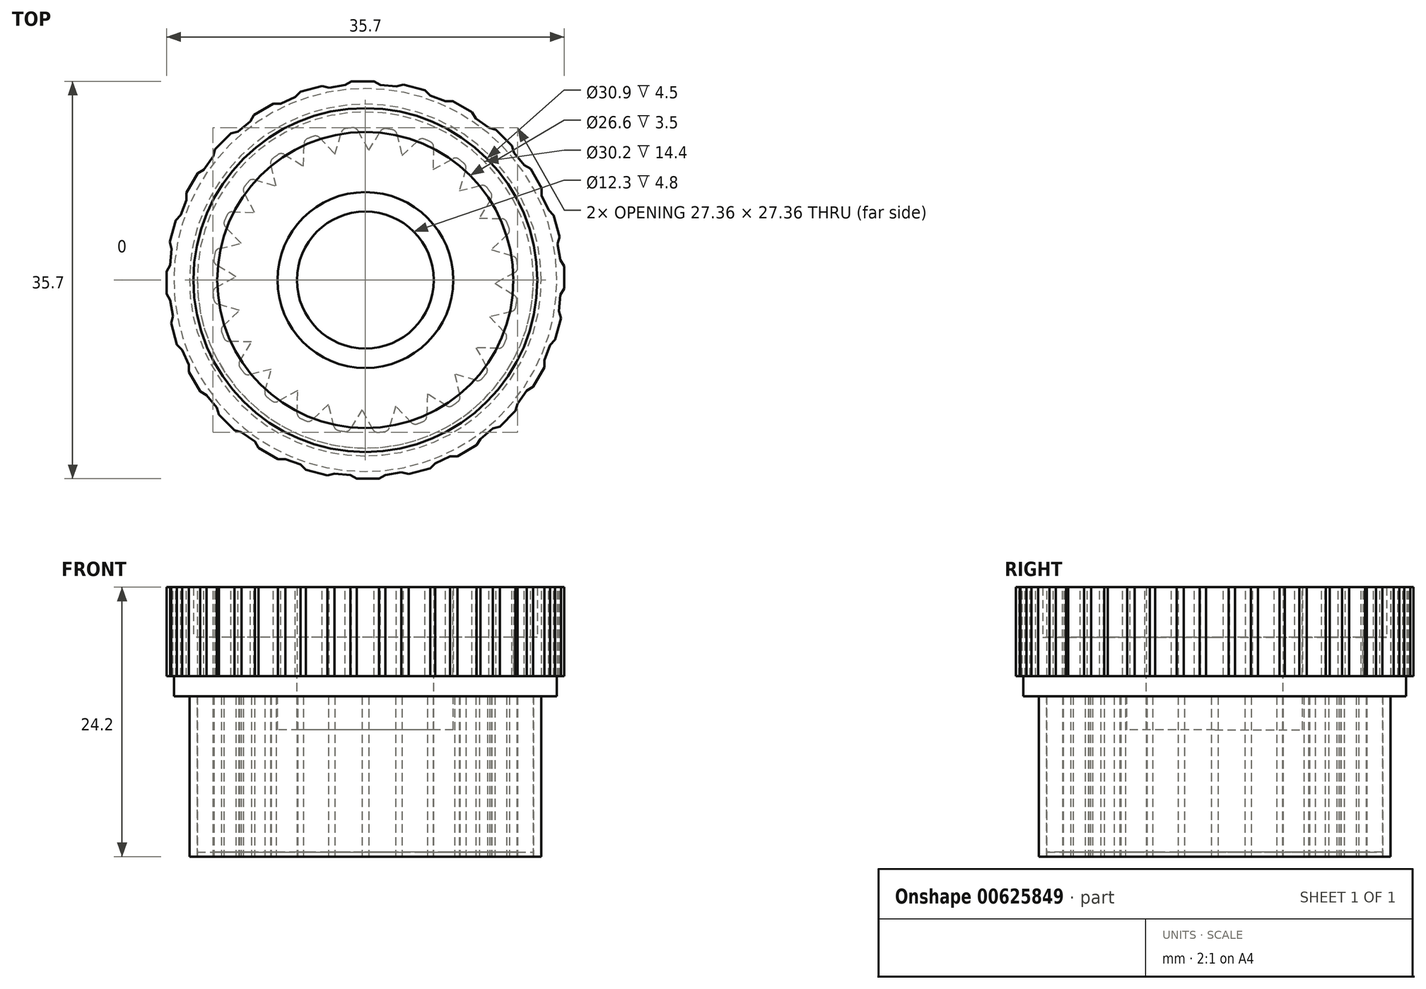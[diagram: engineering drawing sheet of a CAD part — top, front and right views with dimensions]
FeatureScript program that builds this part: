
annotation { "Feature Type Name" : "Feature", "Feature Type Description" : "" }
export const myFeature = defineFeature(function(context is Context, id is Id, definition is map)
    precondition{}
    {
        {
            var Q0;
            Q0=qCreatedBy(makeId("Top.planeOp"),FACE);
            var sketch = newSketch(context, id + "F0", { "sketchPlane" : qUnion([Q0])});
            skCircle(sketch, "E0", {"center": v(0, 0) * mm, "radius": 17.2 * mm});
            skCircle(sketch, "E1", {"center": v(0, 0) * mm, "radius": 15.45 * mm});
            skCircle(sketch, "E2", {"center": v(0, 0) * mm, "radius": 13.3 * mm});
            skCircle(sketch, "E3", {"center": v(0, 0) * mm, "radius": 6.15 * mm});
            skCircle(sketch, "E4", {"center": v(0, 0) * mm, "radius": 7.9 * mm});
            skSolve(sketch);
        }
        {
            var Q0;
            Q0=qSketchRegion(id+"F0",true);
            extrude(context, id + "F1", {"entities" : qUnion([Q0]), "depth" : 8 * mm, "offsetDistance" : 25 * mm});
        }
        {
            var Q0;
            Q0=makeQuery(id+"F0.imprint","IMPRINT",FACE,{"disambiguationData":[TD([[makeQuery(id+"F0.imprint","IMPRINT",EDGE,{"derivedFrom":sQuery(id+"F0.wireOp",EDGE,"E1")}),1.0]])]});
            extrude(context, id + "F2", {"entities" : qUnion([Q0]), "operationType" : NewBodyOperationType.ADD, "depth" : 3.5 * mm, "offsetDistance" : 25 * mm});
        }
        {
            var Q0;
            Q0=makeQuery(id+"F0.imprint","IMPRINT",FACE,{"disambiguationData":[TD([[makeQuery(id+"F0.imprint","IMPRINT",EDGE,{"derivedFrom":sQuery(id+"F0.wireOp",EDGE,"E3")}),-1.0]])]});
            extrude(context, id + "F3", {"entities" : qUnion([Q0]), "depth" : 8 * mm, "offsetDistance" : 25 * mm});
        }
        {
            var Q0;
            Q0=makeQuery(id+"F0.imprint","IMPRINT",FACE,{"disambiguationData":[TD([[makeQuery(id+"F0.imprint","IMPRINT",EDGE,{"derivedFrom":sQuery(id+"F0.wireOp",EDGE,"E0")}),1.0]])]});
            var Q1;
            Q1=makeQuery(id+"F0.imprint","IMPRINT",FACE,{"disambiguationData":[TD([[makeQuery(id+"F0.imprint","IMPRINT",EDGE,{"derivedFrom":sQuery(id+"F0.wireOp",EDGE,"E1")}),1.0]])]});
            var Q2;
            Q2=makeQuery(id+"F0.imprint","IMPRINT",FACE,{"disambiguationData":[TD([[makeQuery(id+"F0.imprint","IMPRINT",EDGE,{"derivedFrom":sQuery(id+"F0.wireOp",EDGE,"E2")}),1.0]])]});
            var Q3;
            Q3=makeQuery(id+"F0.imprint","IMPRINT",FACE,{"disambiguationData":[TD([[makeQuery(id+"F0.imprint","IMPRINT",EDGE,{"derivedFrom":sQuery(id+"F0.wireOp",EDGE,"E3")}),-1.0]])]});
            var Q4;
            Q4=makeQuery(id+"F0.imprint","IMPRINT",FACE,{"disambiguationData":[TD([[makeQuery(id+"F0.imprint","IMPRINT",EDGE,{"derivedFrom":sQuery(id+"F0.wireOp",EDGE,"E3")}),1.0]])]});
            extrude(context, id + "F4", {"entities" : qUnion([Q0, Q1, Q2, Q3, Q4]), "oppositeDirection" : true, "depth" : 1.8 * mm, "offsetDistance" : 25 * mm});
        }
        {
            var Q0;
            Q0=makeQuery(id+"F4.opExtrude","CAP_FACE",FACE,{"disambiguationData":[OSD([sQuery(id+"F0.wireOp",EDGE,"E0")])],"isStart":false});
            var sketch = newSketch(context, id + "F5", { "sketchPlane" : qUnion([Q0])});
            skCircle(sketch, "E5", {"center": v(0, 0) * mm, "radius": 15.8 * mm});
            skCircle(sketch, "E6", {"center": v(0, 0) * mm, "radius": 15.1 * mm});
            skSolve(sketch);
        }
        {
            var Q0;
            Q0=makeQuery(id+"F5.imprint","IMPRINT",FACE,{"disambiguationData":[TD([[makeQuery(id+"F5.imprint","IMPRINT",EDGE,{"derivedFrom":sQuery(id+"F5.wireOp",EDGE,"E5")}),1.0]])]});
            extrude(context, id + "F6", {"entities" : qUnion([Q0]), "operationType" : NewBodyOperationType.ADD, "depth" : 14.4 * mm, "offsetDistance" : 25 * mm});
        }
        {
            var Q0;
            Q0=makeQuery(id+"F6.boolean.opBoolean","SPLIT",FACE,{"disambiguationData":[TD([makeQuery(id+"F6.opExtrude","SWEPT_FACE",FACE,{"disambiguationData":[OSD([sQuery(id+"F5.wireOp",EDGE,"E6")])]})])],"derivedFrom":makeQuery(id+"F4.opExtrude","CAP_FACE",FACE,{"disambiguationData":[OSD([sQuery(id+"F0.wireOp",EDGE,"E0")])],"isStart":false})});
            var sketch = newSketch(context, id + "F7", { "sketchPlane" : qUnion([Q0])});
            skCircle(sketch, "E7", {"center": v(0, 0) * mm, "radius": 6.15 * mm});
            skCircle(sketch, "E8", {"center": v(0, 0) * mm, "radius": 7.9 * mm});
            skSolve(sketch);
        }
        {
            var Q0;
            Q0=qSketchRegion(id+"F7",true);
            extrude(context, id + "F8", {"entities" : qUnion([Q0]), "operationType" : NewBodyOperationType.ADD, "depth" : 3 * mm, "offsetDistance" : 25 * mm});
        }
        {
            var Q0;
            Q0=makeQuery(id+"F8.boolean.opBoolean","SPLIT",FACE,{"disambiguationData":[TD([makeQuery(id+"F8.opExtrude","SWEPT_FACE",FACE,{"disambiguationData":[OSD([sQuery(id+"F7.wireOp",EDGE,"E7")])]})])],"derivedFrom":makeQuery(id+"F6.boolean.opBoolean","SPLIT",FACE,{"disambiguationData":[TD([makeQuery(id+"F6.opExtrude","SWEPT_FACE",FACE,{"disambiguationData":[OSD([sQuery(id+"F5.wireOp",EDGE,"E6")])]})])],"derivedFrom":makeQuery(id+"F4.opExtrude","CAP_FACE",FACE,{"disambiguationData":[OSD([sQuery(id+"F0.wireOp",EDGE,"E0")])],"isStart":false})})});
            extrude(context, id + "F9", {"entities" : qUnion([Q0]), "operationType" : NewBodyOperationType.REMOVE, "oppositeDirection" : true, "depth" : 25 * mm, "offsetDistance" : 25 * mm});
        }
        {
            var Q0;
            Q0=makeQuery(id+"F1.opExtrude","CAP_FACE",FACE,{"disambiguationData":[OSD([sQuery(id+"F0.wireOp",EDGE,"E0"),sQuery(id+"F0.wireOp",EDGE,"E1")])],"isStart":false});
            var sketch = newSketch(context, id + "F10", { "sketchPlane" : qUnion([Q0])});
            skSolve(sketch);
        }
        {
            var Q0;
            Q0=makeQuery(id+"F10.imprint","IMPRINT",FACE,{"disambiguationData":[TD([[makeQuery(id+"F10.imprint","IMPRINT",EDGE,{"derivedFrom":makeQuery(id+"F1.opExtrude","CAP_EDGE",EDGE,{"disambiguationData":[OSD([sQuery(id+"F0.wireOp",EDGE,"E0")])],"isStart":false})}),1.0]])]});
            var sketch = newSketch(context, id + "F11", { "sketchPlane" : qUnion([Q0])});
            skLineSegment(sketch, "E9", {"start": v(-2.39, 17.2) * mm, "end": v(1.91, 17.2) * mm});
            skLineSegment(sketch, "E10", {"start": v(-2.39, 17.2) * mm, "end": v(-1.24, 17.85) * mm});
            skLineSegment(sketch, "E11.MirrorCS", {"start": v(1.91, 17.2) * mm, "end": v(0.77, 17.85) * mm});
            skLineSegment(sketch, "E12", {"start": v(-1.24, 17.85) * mm, "end": v(0.77, 17.85) * mm});
            skLineSegment(sketch, "E13.1.0", {"start": v(-5.82, 16.92) * mm, "end": v(-3.88, 17.44) * mm});
            skLineSegment(sketch, "E13.1.1", {"start": v(-6.76, 16) * mm, "end": v(-2.6, 17.1) * mm});
            skLineSegment(sketch, "E13.1.2", {"start": v(-6.76, 16) * mm, "end": v(-5.82, 16.92) * mm});
            skLineSegment(sketch, "E13.1.3", {"start": v(-2.6, 17.1) * mm, "end": v(-3.88, 17.44) * mm});
            skLineSegment(sketch, "E13.2.0", {"start": v(-10, 14.84) * mm, "end": v(-8.26, 15.84) * mm});
            skLineSegment(sketch, "E13.2.1", {"start": v(-10.67, 13.7) * mm, "end": v(-6.94, 15.85) * mm});
            skLineSegment(sketch, "E13.2.2", {"start": v(-10.67, 13.7) * mm, "end": v(-10, 14.84) * mm});
            skLineSegment(sketch, "E13.2.3", {"start": v(-6.94, 15.85) * mm, "end": v(-8.26, 15.84) * mm});
            skPoint(sketch, "E13.center", {"position": v(0, 0) * mm});
            skLineSegment(sketch, "E14.3.3.0", {"start": v(-13.85, 10.48) * mm, "end": v(-10.8, 13.52) * mm});
            skLineSegment(sketch, "E14.4.3.0", {"start": v(-13.5, 11.75) * mm, "end": v(-12.08, 13.16) * mm});
            skLineSegment(sketch, "E14.6.3.0", {"start": v(-13.85, 10.48) * mm, "end": v(-13.5, 11.75) * mm});
            skLineSegment(sketch, "E14.9.3.0", {"start": v(-10.8, 13.52) * mm, "end": v(-12.08, 13.16) * mm});
            skLineSegment(sketch, "E14.3.4.0", {"start": v(-16.09, 6.53) * mm, "end": v(-13.94, 10.26) * mm});
            skLineSegment(sketch, "E14.4.4.0", {"start": v(-16.08, 7.85) * mm, "end": v(-15.07, 9.59) * mm});
            skLineSegment(sketch, "E14.6.4.0", {"start": v(-16.09, 6.53) * mm, "end": v(-16.08, 7.85) * mm});
            skLineSegment(sketch, "E14.9.4.0", {"start": v(-13.94, 10.26) * mm, "end": v(-15.07, 9.59) * mm});
            skLineSegment(sketch, "E14.3.5.0", {"start": v(-17.23, 2.15) * mm, "end": v(-16.12, 6.3) * mm});
            skLineSegment(sketch, "E14.4.5.0", {"start": v(-17.56, 3.42) * mm, "end": v(-17.04, 5.36) * mm});
            skLineSegment(sketch, "E14.6.5.0", {"start": v(-17.23, 2.15) * mm, "end": v(-17.56, 3.42) * mm});
            skLineSegment(sketch, "E14.9.5.0", {"start": v(-16.12, 6.3) * mm, "end": v(-17.04, 5.36) * mm});
            skLineSegment(sketch, "E14.3.6.0", {"start": v(-17.2, -2.39) * mm, "end": v(-17.2, 1.91) * mm});
            skLineSegment(sketch, "E14.4.6.0", {"start": v(-17.85, -1.24) * mm, "end": v(-17.85, 0.77) * mm});
            skLineSegment(sketch, "E14.6.6.0", {"start": v(-17.2, -2.39) * mm, "end": v(-17.85, -1.24) * mm});
            skLineSegment(sketch, "E14.9.6.0", {"start": v(-17.2, 1.91) * mm, "end": v(-17.85, 0.77) * mm});
            skLineSegment(sketch, "E14.3.7.0", {"start": v(-16, -6.76) * mm, "end": v(-17.1, -2.6) * mm});
            skLineSegment(sketch, "E14.4.7.0", {"start": v(-16.92, -5.82) * mm, "end": v(-17.44, -3.88) * mm});
            skLineSegment(sketch, "E14.6.7.0", {"start": v(-16, -6.76) * mm, "end": v(-16.92, -5.82) * mm});
            skLineSegment(sketch, "E14.9.7.0", {"start": v(-17.1, -2.6) * mm, "end": v(-17.44, -3.88) * mm});
            skLineSegment(sketch, "E14.3.8.0", {"start": v(-13.7, -10.67) * mm, "end": v(-15.85, -6.94) * mm});
            skLineSegment(sketch, "E14.4.8.0", {"start": v(-14.84, -10) * mm, "end": v(-15.84, -8.26) * mm});
            skLineSegment(sketch, "E14.6.8.0", {"start": v(-13.7, -10.67) * mm, "end": v(-14.84, -10) * mm});
            skLineSegment(sketch, "E14.9.8.0", {"start": v(-15.85, -6.94) * mm, "end": v(-15.84, -8.26) * mm});
            skLineSegment(sketch, "E14.3.9.0", {"start": v(-10.48, -13.85) * mm, "end": v(-13.52, -10.8) * mm});
            skLineSegment(sketch, "E14.4.9.0", {"start": v(-11.75, -13.5) * mm, "end": v(-13.16, -12.08) * mm});
            skLineSegment(sketch, "E14.6.9.0", {"start": v(-10.48, -13.85) * mm, "end": v(-11.75, -13.5) * mm});
            skLineSegment(sketch, "E14.9.9.0", {"start": v(-13.52, -10.8) * mm, "end": v(-13.16, -12.08) * mm});
            skLineSegment(sketch, "E14.3.10.0", {"start": v(-6.53, -16.09) * mm, "end": v(-10.26, -13.94) * mm});
            skLineSegment(sketch, "E14.4.10.0", {"start": v(-7.85, -16.08) * mm, "end": v(-9.59, -15.07) * mm});
            skLineSegment(sketch, "E14.6.10.0", {"start": v(-6.53, -16.09) * mm, "end": v(-7.85, -16.08) * mm});
            skLineSegment(sketch, "E14.9.10.0", {"start": v(-10.26, -13.94) * mm, "end": v(-9.59, -15.07) * mm});
            skLineSegment(sketch, "E14.3.11.0", {"start": v(-2.15, -17.23) * mm, "end": v(-6.3, -16.12) * mm});
            skLineSegment(sketch, "E14.4.11.0", {"start": v(-3.42, -17.56) * mm, "end": v(-5.36, -17.04) * mm});
            skLineSegment(sketch, "E14.6.11.0", {"start": v(-2.15, -17.23) * mm, "end": v(-3.42, -17.56) * mm});
            skLineSegment(sketch, "E14.9.11.0", {"start": v(-6.3, -16.12) * mm, "end": v(-5.36, -17.04) * mm});
            skLineSegment(sketch, "E14.3.12.0", {"start": v(2.39, -17.2) * mm, "end": v(-1.91, -17.2) * mm});
            skLineSegment(sketch, "E14.4.12.0", {"start": v(1.24, -17.85) * mm, "end": v(-0.77, -17.85) * mm});
            skLineSegment(sketch, "E14.6.12.0", {"start": v(2.39, -17.2) * mm, "end": v(1.24, -17.85) * mm});
            skLineSegment(sketch, "E14.9.12.0", {"start": v(-1.91, -17.2) * mm, "end": v(-0.77, -17.85) * mm});
            skLineSegment(sketch, "E14.3.13.0", {"start": v(6.76, -16) * mm, "end": v(2.6, -17.1) * mm});
            skLineSegment(sketch, "E14.4.13.0", {"start": v(5.82, -16.92) * mm, "end": v(3.88, -17.44) * mm});
            skLineSegment(sketch, "E14.6.13.0", {"start": v(6.76, -16) * mm, "end": v(5.82, -16.92) * mm});
            skLineSegment(sketch, "E14.9.13.0", {"start": v(2.6, -17.1) * mm, "end": v(3.88, -17.44) * mm});
            skLineSegment(sketch, "E14.3.14.0", {"start": v(10.67, -13.7) * mm, "end": v(6.94, -15.85) * mm});
            skLineSegment(sketch, "E14.4.14.0", {"start": v(10, -14.84) * mm, "end": v(8.26, -15.84) * mm});
            skLineSegment(sketch, "E14.6.14.0", {"start": v(10.67, -13.7) * mm, "end": v(10, -14.84) * mm});
            skLineSegment(sketch, "E14.9.14.0", {"start": v(6.94, -15.85) * mm, "end": v(8.26, -15.84) * mm});
            skLineSegment(sketch, "E14.3.15.0", {"start": v(13.85, -10.48) * mm, "end": v(10.8, -13.52) * mm});
            skLineSegment(sketch, "E14.4.15.0", {"start": v(13.5, -11.75) * mm, "end": v(12.08, -13.16) * mm});
            skLineSegment(sketch, "E14.6.15.0", {"start": v(13.85, -10.48) * mm, "end": v(13.5, -11.75) * mm});
            skLineSegment(sketch, "E14.9.15.0", {"start": v(10.8, -13.52) * mm, "end": v(12.08, -13.16) * mm});
            skLineSegment(sketch, "E14.3.16.0", {"start": v(16.09, -6.53) * mm, "end": v(13.94, -10.26) * mm});
            skLineSegment(sketch, "E14.4.16.0", {"start": v(16.08, -7.85) * mm, "end": v(15.07, -9.59) * mm});
            skLineSegment(sketch, "E14.6.16.0", {"start": v(16.09, -6.53) * mm, "end": v(16.08, -7.85) * mm});
            skLineSegment(sketch, "E14.9.16.0", {"start": v(13.94, -10.26) * mm, "end": v(15.07, -9.59) * mm});
            skLineSegment(sketch, "E14.3.17.0", {"start": v(17.23, -2.15) * mm, "end": v(16.12, -6.3) * mm});
            skLineSegment(sketch, "E14.4.17.0", {"start": v(17.56, -3.42) * mm, "end": v(17.04, -5.36) * mm});
            skLineSegment(sketch, "E14.6.17.0", {"start": v(17.23, -2.15) * mm, "end": v(17.56, -3.42) * mm});
            skLineSegment(sketch, "E14.9.17.0", {"start": v(16.12, -6.3) * mm, "end": v(17.04, -5.36) * mm});
            skLineSegment(sketch, "E14.3.18.0", {"start": v(17.2, 2.39) * mm, "end": v(17.2, -1.91) * mm});
            skLineSegment(sketch, "E14.4.18.0", {"start": v(17.85, 1.24) * mm, "end": v(17.85, -0.77) * mm});
            skLineSegment(sketch, "E14.6.18.0", {"start": v(17.2, 2.39) * mm, "end": v(17.85, 1.24) * mm});
            skLineSegment(sketch, "E14.9.18.0", {"start": v(17.2, -1.91) * mm, "end": v(17.85, -0.77) * mm});
            skLineSegment(sketch, "E14.3.19.0", {"start": v(16, 6.76) * mm, "end": v(17.1, 2.6) * mm});
            skLineSegment(sketch, "E14.4.19.0", {"start": v(16.92, 5.82) * mm, "end": v(17.44, 3.88) * mm});
            skLineSegment(sketch, "E14.6.19.0", {"start": v(16, 6.76) * mm, "end": v(16.92, 5.82) * mm});
            skLineSegment(sketch, "E14.9.19.0", {"start": v(17.1, 2.6) * mm, "end": v(17.44, 3.88) * mm});
            skLineSegment(sketch, "E14.3.20.0", {"start": v(13.7, 10.67) * mm, "end": v(15.85, 6.94) * mm});
            skLineSegment(sketch, "E14.4.20.0", {"start": v(14.84, 10) * mm, "end": v(15.84, 8.26) * mm});
            skLineSegment(sketch, "E14.6.20.0", {"start": v(13.7, 10.67) * mm, "end": v(14.84, 10) * mm});
            skLineSegment(sketch, "E14.9.20.0", {"start": v(15.85, 6.94) * mm, "end": v(15.84, 8.26) * mm});
            skLineSegment(sketch, "E14.3.21.0", {"start": v(10.48, 13.85) * mm, "end": v(13.52, 10.8) * mm});
            skLineSegment(sketch, "E14.4.21.0", {"start": v(11.75, 13.5) * mm, "end": v(13.16, 12.08) * mm});
            skLineSegment(sketch, "E14.6.21.0", {"start": v(10.48, 13.85) * mm, "end": v(11.75, 13.5) * mm});
            skLineSegment(sketch, "E14.9.21.0", {"start": v(13.52, 10.8) * mm, "end": v(13.16, 12.08) * mm});
            skLineSegment(sketch, "E14.3.22.0", {"start": v(6.53, 16.09) * mm, "end": v(10.26, 13.94) * mm});
            skLineSegment(sketch, "E14.4.22.0", {"start": v(7.85, 16.08) * mm, "end": v(9.59, 15.07) * mm});
            skLineSegment(sketch, "E14.6.22.0", {"start": v(6.53, 16.09) * mm, "end": v(7.85, 16.08) * mm});
            skLineSegment(sketch, "E14.9.22.0", {"start": v(10.26, 13.94) * mm, "end": v(9.59, 15.07) * mm});
            skLineSegment(sketch, "E14.3.23.0", {"start": v(2.15, 17.23) * mm, "end": v(6.3, 16.12) * mm});
            skLineSegment(sketch, "E14.4.23.0", {"start": v(3.42, 17.56) * mm, "end": v(5.36, 17.04) * mm});
            skLineSegment(sketch, "E14.6.23.0", {"start": v(2.15, 17.23) * mm, "end": v(3.42, 17.56) * mm});
            skLineSegment(sketch, "E14.9.23.0", {"start": v(6.3, 16.12) * mm, "end": v(5.36, 17.04) * mm});
            skLineSegment(sketch, "E15", {"start": v(-2.6, 17.1) * mm, "end": v(-2.39, 17.2) * mm});
            skLineSegment(sketch, "E16", {"start": v(1.91, 17.2) * mm, "end": v(2.15, 17.23) * mm});
            skLineSegment(sketch, "E17", {"start": v(6.3, 16.12) * mm, "end": v(6.53, 16.09) * mm});
            skLineSegment(sketch, "E18", {"start": v(10.26, 13.94) * mm, "end": v(10.48, 13.85) * mm});
            skLineSegment(sketch, "E19", {"start": v(13.52, 10.8) * mm, "end": v(13.7, 10.67) * mm});
            skLineSegment(sketch, "E20", {"start": v(15.85, 6.94) * mm, "end": v(16, 6.76) * mm});
            skLineSegment(sketch, "E21", {"start": v(17.1, 2.6) * mm, "end": v(17.2, 2.39) * mm});
            skLineSegment(sketch, "E22", {"start": v(17.2, -1.91) * mm, "end": v(17.23, -2.15) * mm});
            skLineSegment(sketch, "E23", {"start": v(16.12, -6.3) * mm, "end": v(16.09, -6.53) * mm});
            skLineSegment(sketch, "E24", {"start": v(13.94, -10.26) * mm, "end": v(13.85, -10.48) * mm});
            skLineSegment(sketch, "E25", {"start": v(10.8, -13.52) * mm, "end": v(10.67, -13.7) * mm});
            skLineSegment(sketch, "E26", {"start": v(6.94, -15.85) * mm, "end": v(6.76, -16) * mm});
            skLineSegment(sketch, "E27", {"start": v(2.6, -17.1) * mm, "end": v(2.39, -17.2) * mm});
            skLineSegment(sketch, "E28", {"start": v(-1.91, -17.2) * mm, "end": v(-2.15, -17.23) * mm});
            skLineSegment(sketch, "E29", {"start": v(-6.3, -16.12) * mm, "end": v(-6.53, -16.09) * mm});
            skLineSegment(sketch, "E30", {"start": v(-10.26, -13.94) * mm, "end": v(-10.48, -13.85) * mm});
            skLineSegment(sketch, "E31", {"start": v(-13.52, -10.8) * mm, "end": v(-13.7, -10.67) * mm});
            skLineSegment(sketch, "E32", {"start": v(-15.85, -6.94) * mm, "end": v(-16, -6.76) * mm});
            skLineSegment(sketch, "E33", {"start": v(-17.2, 1.91) * mm, "end": v(-17.23, 2.15) * mm});
            skLineSegment(sketch, "E34", {"start": v(-16.12, 6.3) * mm, "end": v(-16.09, 6.53) * mm});
            skLineSegment(sketch, "E35", {"start": v(-13.94, 10.26) * mm, "end": v(-13.85, 10.48) * mm});
            skLineSegment(sketch, "E36", {"start": v(-10.8, 13.52) * mm, "end": v(-10.67, 13.7) * mm});
            skLineSegment(sketch, "E37", {"start": v(-6.94, 15.85) * mm, "end": v(-6.76, 16) * mm});
            skLineSegment(sketch, "E38", {"start": v(-3.24, 17.27) * mm, "end": v(-1.81, 17.53) * mm});
            skLineSegment(sketch, "E39", {"start": v(1.34, 17.52) * mm, "end": v(2.79, 17.4) * mm});
            skLineSegment(sketch, "E40", {"start": v(5.83, 16.58) * mm, "end": v(7.2, 16.08) * mm});
            skLineSegment(sketch, "E41", {"start": v(9.92, 14.5) * mm, "end": v(11.11, 13.67) * mm});
            skLineSegment(sketch, "E42", {"start": v(13.34, 11.44) * mm, "end": v(14.27, 10.33) * mm});
            skLineSegment(sketch, "E43", {"start": v(15.85, 7.6) * mm, "end": v(16.46, 6.29) * mm});
            skLineSegment(sketch, "E44", {"start": v(17.27, 3.24) * mm, "end": v(17.53, 1.81) * mm});
            skLineSegment(sketch, "E45", {"start": v(-6.29, 16.46) * mm, "end": v(-7.6, 15.85) * mm});
            skLineSegment(sketch, "E46", {"start": v(-10.33, 14.27) * mm, "end": v(-11.44, 13.34) * mm});
            skLineSegment(sketch, "E47", {"start": v(-13.67, 11.11) * mm, "end": v(-14.5, 9.92) * mm});
            skLineSegment(sketch, "E48", {"start": v(-16.08, 7.2) * mm, "end": v(-16.58, 5.83) * mm});
            skLineSegment(sketch, "E49", {"start": v(-17.2, -2.39) * mm, "end": v(-17.1, -2.6) * mm});
            skLineSegment(sketch, "E50", {"start": v(-17.53, -1.81) * mm, "end": v(-17.27, -3.24) * mm});
            skLineSegment(sketch, "E51", {"start": v(-16.46, -6.29) * mm, "end": v(-15.85, -7.6) * mm});
            skLineSegment(sketch, "E52", {"start": v(-14.27, -10.33) * mm, "end": v(-13.34, -11.44) * mm});
            skLineSegment(sketch, "E53", {"start": v(-11.11, -13.67) * mm, "end": v(-9.92, -14.5) * mm});
            skLineSegment(sketch, "E54", {"start": v(-7.2, -16.08) * mm, "end": v(-5.83, -16.58) * mm});
            skLineSegment(sketch, "E55", {"start": v(-2.79, -17.4) * mm, "end": v(-1.34, -17.52) * mm});
            skLineSegment(sketch, "E56", {"start": v(1.81, -17.52) * mm, "end": v(3.24, -17.27) * mm});
            skLineSegment(sketch, "E57", {"start": v(6.29, -16.46) * mm, "end": v(7.6, -15.85) * mm});
            skLineSegment(sketch, "E58", {"start": v(10.33, -14.27) * mm, "end": v(11.44, -13.34) * mm});
            skLineSegment(sketch, "E59", {"start": v(13.67, -11.11) * mm, "end": v(14.5, -9.92) * mm});
            skLineSegment(sketch, "E60", {"start": v(16.08, -7.2) * mm, "end": v(16.58, -5.83) * mm});
            skLineSegment(sketch, "E61", {"start": v(17.4, -2.79) * mm, "end": v(17.52, -1.34) * mm});
            skLineSegment(sketch, "E62", {"start": v(-17.4, 2.79) * mm, "end": v(-17.52, 1.34) * mm});
            skSolve(sketch);
        }
        {
            var Q0;
            {var subQ4=sQuery(id+"F11.wireOp",EDGE,"E14.4.5.0");Q0=makeQuery(id+"F11.imprint","IMPRINT",FACE,{"disambiguationData":[TD([[makeQuery(id+"F11.imprint","IMPRINT",EDGE,{"derivedFrom":subQ4}),-1.0]])]});}
            var Q1;
            {var subQ0=sQuery(id+"F11.wireOp",EDGE,"E33");Q1=makeQuery(id+"F11.imprint","IMPRINT",FACE,{"disambiguationData":[TD([[makeQuery(id+"F11.imprint","IMPRINT",EDGE,{"derivedFrom":subQ0}),1.0]])]});}
            var Q2;
            {var subQ0=sQuery(id+"F11.wireOp",EDGE,"E33");Q2=makeQuery(id+"F11.imprint","IMPRINT",FACE,{"disambiguationData":[TD([[makeQuery(id+"F11.imprint","IMPRINT",EDGE,{"derivedFrom":subQ0}),-1.0]])]});}
            var Q3;
            {var subQ4=sQuery(id+"F11.wireOp",EDGE,"E14.4.6.0");Q3=makeQuery(id+"F11.imprint","IMPRINT",FACE,{"disambiguationData":[TD([[makeQuery(id+"F11.imprint","IMPRINT",EDGE,{"derivedFrom":subQ4}),-1.0]])]});}
            var Q4;
            {var subQ0=sQuery(id+"F11.wireOp",EDGE,"E49");Q4=makeQuery(id+"F11.imprint","IMPRINT",FACE,{"disambiguationData":[TD([[makeQuery(id+"F11.imprint","IMPRINT",EDGE,{"derivedFrom":subQ0}),-1.0]])]});}
            var Q5;
            {var subQ4=sQuery(id+"F11.wireOp",EDGE,"E14.4.7.0");Q5=makeQuery(id+"F11.imprint","IMPRINT",FACE,{"disambiguationData":[TD([[makeQuery(id+"F11.imprint","IMPRINT",EDGE,{"derivedFrom":subQ4}),-1.0]])]});}
            var Q6;
            {var subQ0=sQuery(id+"F11.wireOp",EDGE,"E49");Q6=makeQuery(id+"F11.imprint","IMPRINT",FACE,{"disambiguationData":[TD([[makeQuery(id+"F11.imprint","IMPRINT",EDGE,{"derivedFrom":subQ0}),1.0]])]});}
            var Q7;
            {var subQ0=sQuery(id+"F11.wireOp",EDGE,"E32");Q7=makeQuery(id+"F11.imprint","IMPRINT",FACE,{"disambiguationData":[TD([[makeQuery(id+"F11.imprint","IMPRINT",EDGE,{"derivedFrom":subQ0}),-1.0]])]});}
            var Q8;
            {var subQ0=sQuery(id+"F11.wireOp",EDGE,"E32");Q8=makeQuery(id+"F11.imprint","IMPRINT",FACE,{"disambiguationData":[TD([[makeQuery(id+"F11.imprint","IMPRINT",EDGE,{"derivedFrom":subQ0}),1.0]])]});}
            var Q9;
            {var subQ4=sQuery(id+"F11.wireOp",EDGE,"E14.4.8.0");Q9=makeQuery(id+"F11.imprint","IMPRINT",FACE,{"disambiguationData":[TD([[makeQuery(id+"F11.imprint","IMPRINT",EDGE,{"derivedFrom":subQ4}),-1.0]])]});}
            var Q10;
            {var subQ0=sQuery(id+"F11.wireOp",EDGE,"E31");Q10=makeQuery(id+"F11.imprint","IMPRINT",FACE,{"disambiguationData":[TD([[makeQuery(id+"F11.imprint","IMPRINT",EDGE,{"derivedFrom":subQ0}),-1.0]])]});}
            var Q11;
            {var subQ0=sQuery(id+"F11.wireOp",EDGE,"E31");Q11=makeQuery(id+"F11.imprint","IMPRINT",FACE,{"disambiguationData":[TD([[makeQuery(id+"F11.imprint","IMPRINT",EDGE,{"derivedFrom":subQ0}),1.0]])]});}
            var Q12;
            {var subQ4=sQuery(id+"F11.wireOp",EDGE,"E14.4.9.0");Q12=makeQuery(id+"F11.imprint","IMPRINT",FACE,{"disambiguationData":[TD([[makeQuery(id+"F11.imprint","IMPRINT",EDGE,{"derivedFrom":subQ4}),-1.0]])]});}
            var Q13;
            {var subQ0=sQuery(id+"F11.wireOp",EDGE,"E30");Q13=makeQuery(id+"F11.imprint","IMPRINT",FACE,{"disambiguationData":[TD([[makeQuery(id+"F11.imprint","IMPRINT",EDGE,{"derivedFrom":subQ0}),-1.0]])]});}
            var Q14;
            {var subQ0=sQuery(id+"F11.wireOp",EDGE,"E30");Q14=makeQuery(id+"F11.imprint","IMPRINT",FACE,{"disambiguationData":[TD([[makeQuery(id+"F11.imprint","IMPRINT",EDGE,{"derivedFrom":subQ0}),1.0]])]});}
            var Q15;
            {var subQ4=sQuery(id+"F11.wireOp",EDGE,"E14.4.10.0");Q15=makeQuery(id+"F11.imprint","IMPRINT",FACE,{"disambiguationData":[TD([[makeQuery(id+"F11.imprint","IMPRINT",EDGE,{"derivedFrom":subQ4}),-1.0]])]});}
            var Q16;
            {var subQ4=sQuery(id+"F11.wireOp",EDGE,"E14.4.11.0");Q16=makeQuery(id+"F11.imprint","IMPRINT",FACE,{"disambiguationData":[TD([[makeQuery(id+"F11.imprint","IMPRINT",EDGE,{"derivedFrom":subQ4}),-1.0]])]});}
            var Q17;
            {var subQ0=sQuery(id+"F11.wireOp",EDGE,"E29");Q17=makeQuery(id+"F11.imprint","IMPRINT",FACE,{"disambiguationData":[TD([[makeQuery(id+"F11.imprint","IMPRINT",EDGE,{"derivedFrom":subQ0}),1.0]])]});}
            var Q18;
            {var subQ0=sQuery(id+"F11.wireOp",EDGE,"E29");Q18=makeQuery(id+"F11.imprint","IMPRINT",FACE,{"disambiguationData":[TD([[makeQuery(id+"F11.imprint","IMPRINT",EDGE,{"derivedFrom":subQ0}),-1.0]])]});}
            var Q19;
            {var subQ0=sQuery(id+"F11.wireOp",EDGE,"E28");Q19=makeQuery(id+"F11.imprint","IMPRINT",FACE,{"disambiguationData":[TD([[makeQuery(id+"F11.imprint","IMPRINT",EDGE,{"derivedFrom":subQ0}),-1.0]])]});}
            var Q20;
            {var subQ4=sQuery(id+"F11.wireOp",EDGE,"E14.4.12.0");Q20=makeQuery(id+"F11.imprint","IMPRINT",FACE,{"disambiguationData":[TD([[makeQuery(id+"F11.imprint","IMPRINT",EDGE,{"derivedFrom":subQ4}),-1.0]])]});}
            var Q21;
            {var subQ0=sQuery(id+"F11.wireOp",EDGE,"E28");Q21=makeQuery(id+"F11.imprint","IMPRINT",FACE,{"disambiguationData":[TD([[makeQuery(id+"F11.imprint","IMPRINT",EDGE,{"derivedFrom":subQ0}),1.0]])]});}
            var Q22;
            {var subQ0=sQuery(id+"F11.wireOp",EDGE,"E27");Q22=makeQuery(id+"F11.imprint","IMPRINT",FACE,{"disambiguationData":[TD([[makeQuery(id+"F11.imprint","IMPRINT",EDGE,{"derivedFrom":subQ0}),-1.0]])]});}
            var Q23;
            {var subQ0=sQuery(id+"F11.wireOp",EDGE,"E27");Q23=makeQuery(id+"F11.imprint","IMPRINT",FACE,{"disambiguationData":[TD([[makeQuery(id+"F11.imprint","IMPRINT",EDGE,{"derivedFrom":subQ0}),1.0]])]});}
            var Q24;
            {var subQ4=sQuery(id+"F11.wireOp",EDGE,"E14.4.13.0");Q24=makeQuery(id+"F11.imprint","IMPRINT",FACE,{"disambiguationData":[TD([[makeQuery(id+"F11.imprint","IMPRINT",EDGE,{"derivedFrom":subQ4}),-1.0]])]});}
            var Q25;
            {var subQ0=sQuery(id+"F11.wireOp",EDGE,"E26");Q25=makeQuery(id+"F11.imprint","IMPRINT",FACE,{"disambiguationData":[TD([[makeQuery(id+"F11.imprint","IMPRINT",EDGE,{"derivedFrom":subQ0}),-1.0]])]});}
            var Q26;
            {var subQ0=sQuery(id+"F11.wireOp",EDGE,"E26");Q26=makeQuery(id+"F11.imprint","IMPRINT",FACE,{"disambiguationData":[TD([[makeQuery(id+"F11.imprint","IMPRINT",EDGE,{"derivedFrom":subQ0}),1.0]])]});}
            var Q27;
            {var subQ4=sQuery(id+"F11.wireOp",EDGE,"E14.4.14.0");Q27=makeQuery(id+"F11.imprint","IMPRINT",FACE,{"disambiguationData":[TD([[makeQuery(id+"F11.imprint","IMPRINT",EDGE,{"derivedFrom":subQ4}),-1.0]])]});}
            var Q28;
            {var subQ4=sQuery(id+"F11.wireOp",EDGE,"E14.4.15.0");Q28=makeQuery(id+"F11.imprint","IMPRINT",FACE,{"disambiguationData":[TD([[makeQuery(id+"F11.imprint","IMPRINT",EDGE,{"derivedFrom":subQ4}),-1.0]])]});}
            var Q29;
            {var subQ0=sQuery(id+"F11.wireOp",EDGE,"E25");Q29=makeQuery(id+"F11.imprint","IMPRINT",FACE,{"disambiguationData":[TD([[makeQuery(id+"F11.imprint","IMPRINT",EDGE,{"derivedFrom":subQ0}),1.0]])]});}
            var Q30;
            {var subQ0=sQuery(id+"F11.wireOp",EDGE,"E25");Q30=makeQuery(id+"F11.imprint","IMPRINT",FACE,{"disambiguationData":[TD([[makeQuery(id+"F11.imprint","IMPRINT",EDGE,{"derivedFrom":subQ0}),-1.0]])]});}
            var Q31;
            {var subQ0=sQuery(id+"F11.wireOp",EDGE,"E24");Q31=makeQuery(id+"F11.imprint","IMPRINT",FACE,{"disambiguationData":[TD([[makeQuery(id+"F11.imprint","IMPRINT",EDGE,{"derivedFrom":subQ0}),-1.0]])]});}
            var Q32;
            {var subQ0=sQuery(id+"F11.wireOp",EDGE,"E24");Q32=makeQuery(id+"F11.imprint","IMPRINT",FACE,{"disambiguationData":[TD([[makeQuery(id+"F11.imprint","IMPRINT",EDGE,{"derivedFrom":subQ0}),1.0]])]});}
            var Q33;
            {var subQ4=sQuery(id+"F11.wireOp",EDGE,"E14.4.16.0");Q33=makeQuery(id+"F11.imprint","IMPRINT",FACE,{"disambiguationData":[TD([[makeQuery(id+"F11.imprint","IMPRINT",EDGE,{"derivedFrom":subQ4}),-1.0]])]});}
            var Q34;
            {var subQ0=sQuery(id+"F11.wireOp",EDGE,"E23");Q34=makeQuery(id+"F11.imprint","IMPRINT",FACE,{"disambiguationData":[TD([[makeQuery(id+"F11.imprint","IMPRINT",EDGE,{"derivedFrom":subQ0}),-1.0]])]});}
            var Q35;
            {var subQ0=sQuery(id+"F11.wireOp",EDGE,"E23");Q35=makeQuery(id+"F11.imprint","IMPRINT",FACE,{"disambiguationData":[TD([[makeQuery(id+"F11.imprint","IMPRINT",EDGE,{"derivedFrom":subQ0}),1.0]])]});}
            var Q36;
            {var subQ4=sQuery(id+"F11.wireOp",EDGE,"E14.4.17.0");Q36=makeQuery(id+"F11.imprint","IMPRINT",FACE,{"disambiguationData":[TD([[makeQuery(id+"F11.imprint","IMPRINT",EDGE,{"derivedFrom":subQ4}),-1.0]])]});}
            var Q37;
            {var subQ0=sQuery(id+"F11.wireOp",EDGE,"E22");Q37=makeQuery(id+"F11.imprint","IMPRINT",FACE,{"disambiguationData":[TD([[makeQuery(id+"F11.imprint","IMPRINT",EDGE,{"derivedFrom":subQ0}),-1.0]])]});}
            var Q38;
            {var subQ0=sQuery(id+"F11.wireOp",EDGE,"E22");Q38=makeQuery(id+"F11.imprint","IMPRINT",FACE,{"disambiguationData":[TD([[makeQuery(id+"F11.imprint","IMPRINT",EDGE,{"derivedFrom":subQ0}),1.0]])]});}
            var Q39;
            {var subQ4=sQuery(id+"F11.wireOp",EDGE,"E14.4.18.0");Q39=makeQuery(id+"F11.imprint","IMPRINT",FACE,{"disambiguationData":[TD([[makeQuery(id+"F11.imprint","IMPRINT",EDGE,{"derivedFrom":subQ4}),-1.0]])]});}
            var Q40;
            {var subQ0=sQuery(id+"F11.wireOp",EDGE,"E21");Q40=makeQuery(id+"F11.imprint","IMPRINT",FACE,{"disambiguationData":[TD([[makeQuery(id+"F11.imprint","IMPRINT",EDGE,{"derivedFrom":subQ0}),-1.0]])]});}
            var Q41;
            {var subQ0=sQuery(id+"F11.wireOp",EDGE,"E21");Q41=makeQuery(id+"F11.imprint","IMPRINT",FACE,{"disambiguationData":[TD([[makeQuery(id+"F11.imprint","IMPRINT",EDGE,{"derivedFrom":subQ0}),1.0]])]});}
            var Q42;
            {var subQ4=sQuery(id+"F11.wireOp",EDGE,"E14.4.19.0");Q42=makeQuery(id+"F11.imprint","IMPRINT",FACE,{"disambiguationData":[TD([[makeQuery(id+"F11.imprint","IMPRINT",EDGE,{"derivedFrom":subQ4}),-1.0]])]});}
            var Q43;
            {var subQ0=sQuery(id+"F11.wireOp",EDGE,"E20");Q43=makeQuery(id+"F11.imprint","IMPRINT",FACE,{"disambiguationData":[TD([[makeQuery(id+"F11.imprint","IMPRINT",EDGE,{"derivedFrom":subQ0}),-1.0]])]});}
            var Q44;
            {var subQ0=sQuery(id+"F11.wireOp",EDGE,"E20");Q44=makeQuery(id+"F11.imprint","IMPRINT",FACE,{"disambiguationData":[TD([[makeQuery(id+"F11.imprint","IMPRINT",EDGE,{"derivedFrom":subQ0}),1.0]])]});}
            var Q45;
            {var subQ4=sQuery(id+"F11.wireOp",EDGE,"E14.4.20.0");Q45=makeQuery(id+"F11.imprint","IMPRINT",FACE,{"disambiguationData":[TD([[makeQuery(id+"F11.imprint","IMPRINT",EDGE,{"derivedFrom":subQ4}),-1.0]])]});}
            var Q46;
            {var subQ0=sQuery(id+"F11.wireOp",EDGE,"E19");Q46=makeQuery(id+"F11.imprint","IMPRINT",FACE,{"disambiguationData":[TD([[makeQuery(id+"F11.imprint","IMPRINT",EDGE,{"derivedFrom":subQ0}),-1.0]])]});}
            var Q47;
            {var subQ0=sQuery(id+"F11.wireOp",EDGE,"E19");Q47=makeQuery(id+"F11.imprint","IMPRINT",FACE,{"disambiguationData":[TD([[makeQuery(id+"F11.imprint","IMPRINT",EDGE,{"derivedFrom":subQ0}),1.0]])]});}
            var Q48;
            {var subQ4=sQuery(id+"F11.wireOp",EDGE,"E14.4.21.0");Q48=makeQuery(id+"F11.imprint","IMPRINT",FACE,{"disambiguationData":[TD([[makeQuery(id+"F11.imprint","IMPRINT",EDGE,{"derivedFrom":subQ4}),-1.0]])]});}
            var Q49;
            {var subQ0=sQuery(id+"F11.wireOp",EDGE,"E18");Q49=makeQuery(id+"F11.imprint","IMPRINT",FACE,{"disambiguationData":[TD([[makeQuery(id+"F11.imprint","IMPRINT",EDGE,{"derivedFrom":subQ0}),-1.0]])]});}
            var Q50;
            {var subQ0=sQuery(id+"F11.wireOp",EDGE,"E18");Q50=makeQuery(id+"F11.imprint","IMPRINT",FACE,{"disambiguationData":[TD([[makeQuery(id+"F11.imprint","IMPRINT",EDGE,{"derivedFrom":subQ0}),1.0]])]});}
            var Q51;
            {var subQ4=sQuery(id+"F11.wireOp",EDGE,"E14.4.22.0");Q51=makeQuery(id+"F11.imprint","IMPRINT",FACE,{"disambiguationData":[TD([[makeQuery(id+"F11.imprint","IMPRINT",EDGE,{"derivedFrom":subQ4}),-1.0]])]});}
            var Q52;
            {var subQ0=sQuery(id+"F11.wireOp",EDGE,"E17");Q52=makeQuery(id+"F11.imprint","IMPRINT",FACE,{"disambiguationData":[TD([[makeQuery(id+"F11.imprint","IMPRINT",EDGE,{"derivedFrom":subQ0}),-1.0]])]});}
            var Q53;
            {var subQ0=sQuery(id+"F11.wireOp",EDGE,"E17");Q53=makeQuery(id+"F11.imprint","IMPRINT",FACE,{"disambiguationData":[TD([[makeQuery(id+"F11.imprint","IMPRINT",EDGE,{"derivedFrom":subQ0}),1.0]])]});}
            var Q54;
            {var subQ4=sQuery(id+"F11.wireOp",EDGE,"E14.4.23.0");Q54=makeQuery(id+"F11.imprint","IMPRINT",FACE,{"disambiguationData":[TD([[makeQuery(id+"F11.imprint","IMPRINT",EDGE,{"derivedFrom":subQ4}),-1.0]])]});}
            var Q55;
            {var subQ0=sQuery(id+"F11.wireOp",EDGE,"E16");Q55=makeQuery(id+"F11.imprint","IMPRINT",FACE,{"disambiguationData":[TD([[makeQuery(id+"F11.imprint","IMPRINT",EDGE,{"derivedFrom":subQ0}),-1.0]])]});}
            var Q56;
            {var subQ0=sQuery(id+"F11.wireOp",EDGE,"E16");Q56=makeQuery(id+"F11.imprint","IMPRINT",FACE,{"disambiguationData":[TD([[makeQuery(id+"F11.imprint","IMPRINT",EDGE,{"derivedFrom":subQ0}),1.0]])]});}
            var Q57;
            {var subQ0=sQuery(id+"F11.wireOp",EDGE,"E12");Q57=makeQuery(id+"F11.imprint","IMPRINT",FACE,{"disambiguationData":[TD([[makeQuery(id+"F11.imprint","IMPRINT",EDGE,{"derivedFrom":subQ0}),-1.0]])]});}
            var Q58;
            {var subQ0=sQuery(id+"F11.wireOp",EDGE,"E15");Q58=makeQuery(id+"F11.imprint","IMPRINT",FACE,{"disambiguationData":[TD([[makeQuery(id+"F11.imprint","IMPRINT",EDGE,{"derivedFrom":subQ0}),-1.0]])]});}
            var Q59;
            {var subQ0=sQuery(id+"F11.wireOp",EDGE,"E15");Q59=makeQuery(id+"F11.imprint","IMPRINT",FACE,{"disambiguationData":[TD([[makeQuery(id+"F11.imprint","IMPRINT",EDGE,{"derivedFrom":subQ0}),1.0]])]});}
            var Q60;
            {var subQ7=sQuery(id+"F11.wireOp",EDGE,"E13.1.0");Q60=makeQuery(id+"F11.imprint","IMPRINT",FACE,{"disambiguationData":[TD([[makeQuery(id+"F11.imprint","IMPRINT",EDGE,{"derivedFrom":subQ7}),-1.0]])]});}
            var Q61;
            {var subQ0=sQuery(id+"F11.wireOp",EDGE,"E37");Q61=makeQuery(id+"F11.imprint","IMPRINT",FACE,{"disambiguationData":[TD([[makeQuery(id+"F11.imprint","IMPRINT",EDGE,{"derivedFrom":subQ0}),-1.0]])]});}
            var Q62;
            {var subQ0=sQuery(id+"F11.wireOp",EDGE,"E37");Q62=makeQuery(id+"F11.imprint","IMPRINT",FACE,{"disambiguationData":[TD([[makeQuery(id+"F11.imprint","IMPRINT",EDGE,{"derivedFrom":subQ0}),1.0]])]});}
            var Q63;
            {var subQ7=sQuery(id+"F11.wireOp",EDGE,"E13.2.0");Q63=makeQuery(id+"F11.imprint","IMPRINT",FACE,{"disambiguationData":[TD([[makeQuery(id+"F11.imprint","IMPRINT",EDGE,{"derivedFrom":subQ7}),-1.0]])]});}
            var Q64;
            {var subQ0=sQuery(id+"F11.wireOp",EDGE,"E36");Q64=makeQuery(id+"F11.imprint","IMPRINT",FACE,{"disambiguationData":[TD([[makeQuery(id+"F11.imprint","IMPRINT",EDGE,{"derivedFrom":subQ0}),-1.0]])]});}
            var Q65;
            {var subQ0=sQuery(id+"F11.wireOp",EDGE,"E36");Q65=makeQuery(id+"F11.imprint","IMPRINT",FACE,{"disambiguationData":[TD([[makeQuery(id+"F11.imprint","IMPRINT",EDGE,{"derivedFrom":subQ0}),1.0]])]});}
            var Q66;
            {var subQ4=sQuery(id+"F11.wireOp",EDGE,"E14.4.3.0");Q66=makeQuery(id+"F11.imprint","IMPRINT",FACE,{"disambiguationData":[TD([[makeQuery(id+"F11.imprint","IMPRINT",EDGE,{"derivedFrom":subQ4}),-1.0]])]});}
            var Q67;
            {var subQ0=sQuery(id+"F11.wireOp",EDGE,"E35");Q67=makeQuery(id+"F11.imprint","IMPRINT",FACE,{"disambiguationData":[TD([[makeQuery(id+"F11.imprint","IMPRINT",EDGE,{"derivedFrom":subQ0}),-1.0]])]});}
            var Q68;
            {var subQ0=sQuery(id+"F11.wireOp",EDGE,"E35");Q68=makeQuery(id+"F11.imprint","IMPRINT",FACE,{"disambiguationData":[TD([[makeQuery(id+"F11.imprint","IMPRINT",EDGE,{"derivedFrom":subQ0}),1.0]])]});}
            var Q69;
            {var subQ4=sQuery(id+"F11.wireOp",EDGE,"E14.4.4.0");Q69=makeQuery(id+"F11.imprint","IMPRINT",FACE,{"disambiguationData":[TD([[makeQuery(id+"F11.imprint","IMPRINT",EDGE,{"derivedFrom":subQ4}),-1.0]])]});}
            var Q70;
            {var subQ0=sQuery(id+"F11.wireOp",EDGE,"E34");Q70=makeQuery(id+"F11.imprint","IMPRINT",FACE,{"disambiguationData":[TD([[makeQuery(id+"F11.imprint","IMPRINT",EDGE,{"derivedFrom":subQ0}),-1.0]])]});}
            var Q71;
            {var subQ0=sQuery(id+"F11.wireOp",EDGE,"E34");Q71=makeQuery(id+"F11.imprint","IMPRINT",FACE,{"disambiguationData":[TD([[makeQuery(id+"F11.imprint","IMPRINT",EDGE,{"derivedFrom":subQ0}),1.0]])]});}
            extrude(context, id + "F12", {"entities" : qUnion([Q0, Q1, Q2, Q3, Q4, Q5, Q6, Q7, Q8, Q9, Q10, Q11, Q12, Q13, Q14, Q15, Q16, Q17, Q18, Q19, Q20, Q21, Q22, Q23, Q24, Q25, Q26, Q27, Q28, Q29, Q30, Q31, Q32, Q33, Q34, Q35, Q36, Q37, Q38, Q39, Q40, Q41, Q42, Q43, Q44, Q45, Q46, Q47, Q48, Q49, Q50, Q51, Q52, Q53, Q54, Q55, Q56, Q57, Q58, Q59, Q60, Q61, Q62, Q63, Q64, Q65, Q66, Q67, Q68, Q69, Q70, Q71]), "operationType" : NewBodyOperationType.ADD, "oppositeDirection" : true, "depth" : 8 * mm, "offsetDistance" : 25 * mm});
        }
        {
            var Q0;
            Q0=makeQuery(id+"F6.opExtrude","CAP_FACE",FACE,{"disambiguationData":[OSD([sQuery(id+"F5.wireOp",EDGE,"E5"),sQuery(id+"F5.wireOp",EDGE,"E6")])],"isStart":false});
            var sketch = newSketch(context, id + "F13", { "sketchPlane" : qUnion([Q0])});
            skLineSegment(sketch, "E63.0", {"start": v(-0.3, 11.64) * mm, "end": v(-1.35, 13.37) * mm});
            skLineSegment(sketch, "E63.2", {"start": v(0.67, 13.42) * mm, "end": v(-0.3, 11.64) * mm});
            skLineSegment(sketch, "E64.1.0", {"start": v(-2.83, 13.14) * mm, "end": v(-3.3, 11.17) * mm});
            skLineSegment(sketch, "E64.1.2", {"start": v(-3.3, 11.17) * mm, "end": v(-4.77, 12.56) * mm});
            skLineSegment(sketch, "E64.2.0", {"start": v(-6.13, 11.96) * mm, "end": v(-6.08, 9.93) * mm});
            skLineSegment(sketch, "E64.2.2", {"start": v(-6.08, 9.93) * mm, "end": v(-7.86, 10.9) * mm});
            skLineSegment(sketch, "E64.3.0", {"start": v(-9.02, 9.97) * mm, "end": v(-8.44, 8.02) * mm});
            skLineSegment(sketch, "E64.3.2", {"start": v(-8.44, 8.02) * mm, "end": v(-10.41, 8.5) * mm});
            skLineSegment(sketch, "E64.4.0", {"start": v(-11.29, 7.3) * mm, "end": v(-10.23, 5.56) * mm});
            skLineSegment(sketch, "E64.4.2", {"start": v(-10.23, 5.56) * mm, "end": v(-12.26, 5.51) * mm});
            skLineSegment(sketch, "E64.5.0", {"start": v(-12.8, 4.12) * mm, "end": v(-11.32, 2.73) * mm});
            skLineSegment(sketch, "E64.5.2", {"start": v(-11.32, 2.73) * mm, "end": v(-13.26, 2.15) * mm});
            skLineSegment(sketch, "E64.6.0", {"start": v(-13.42, 0.67) * mm, "end": v(-11.64, -0.3) * mm});
            skLineSegment(sketch, "E64.6.2", {"start": v(-11.64, -0.3) * mm, "end": v(-13.37, -1.35) * mm});
            skLineSegment(sketch, "E64.7.0", {"start": v(-13.14, -2.83) * mm, "end": v(-11.17, -3.3) * mm});
            skLineSegment(sketch, "E64.7.2", {"start": v(-11.17, -3.3) * mm, "end": v(-12.56, -4.77) * mm});
            skLineSegment(sketch, "E64.8.0", {"start": v(-11.96, -6.13) * mm, "end": v(-9.93, -6.08) * mm});
            skLineSegment(sketch, "E64.8.2", {"start": v(-9.93, -6.08) * mm, "end": v(-10.9, -7.86) * mm});
            skLineSegment(sketch, "E64.9.0", {"start": v(-9.97, -9.02) * mm, "end": v(-8.02, -8.44) * mm});
            skLineSegment(sketch, "E64.9.2", {"start": v(-8.02, -8.44) * mm, "end": v(-8.5, -10.41) * mm});
            skLineSegment(sketch, "E64.10.0", {"start": v(-7.3, -11.29) * mm, "end": v(-5.56, -10.23) * mm});
            skLineSegment(sketch, "E64.10.2", {"start": v(-5.56, -10.23) * mm, "end": v(-5.51, -12.26) * mm});
            skLineSegment(sketch, "E64.11.0", {"start": v(-4.12, -12.8) * mm, "end": v(-2.73, -11.32) * mm});
            skLineSegment(sketch, "E64.11.2", {"start": v(-2.73, -11.32) * mm, "end": v(-2.15, -13.26) * mm});
            skLineSegment(sketch, "E64.12.0", {"start": v(-0.67, -13.42) * mm, "end": v(0.3, -11.64) * mm});
            skLineSegment(sketch, "E64.12.2", {"start": v(0.3, -11.64) * mm, "end": v(1.35, -13.37) * mm});
            skLineSegment(sketch, "E64.13.0", {"start": v(2.83, -13.14) * mm, "end": v(3.3, -11.17) * mm});
            skLineSegment(sketch, "E64.13.2", {"start": v(3.3, -11.17) * mm, "end": v(4.77, -12.56) * mm});
            skLineSegment(sketch, "E64.14.0", {"start": v(6.13, -11.96) * mm, "end": v(6.08, -9.93) * mm});
            skLineSegment(sketch, "E64.14.2", {"start": v(6.08, -9.93) * mm, "end": v(7.86, -10.9) * mm});
            skLineSegment(sketch, "E64.15.0", {"start": v(9.02, -9.97) * mm, "end": v(8.44, -8.02) * mm});
            skLineSegment(sketch, "E64.15.2", {"start": v(8.44, -8.02) * mm, "end": v(10.41, -8.5) * mm});
            skLineSegment(sketch, "E64.16.0", {"start": v(11.29, -7.3) * mm, "end": v(10.23, -5.56) * mm});
            skLineSegment(sketch, "E64.16.2", {"start": v(10.23, -5.56) * mm, "end": v(12.26, -5.51) * mm});
            skLineSegment(sketch, "E64.17.0", {"start": v(12.8, -4.12) * mm, "end": v(11.32, -2.73) * mm});
            skLineSegment(sketch, "E64.17.2", {"start": v(11.32, -2.73) * mm, "end": v(13.26, -2.15) * mm});
            skLineSegment(sketch, "E64.18.0", {"start": v(13.42, -0.67) * mm, "end": v(11.64, 0.3) * mm});
            skLineSegment(sketch, "E64.18.2", {"start": v(11.64, 0.3) * mm, "end": v(13.37, 1.35) * mm});
            skLineSegment(sketch, "E64.19.0", {"start": v(13.14, 2.83) * mm, "end": v(11.17, 3.3) * mm});
            skLineSegment(sketch, "E64.19.2", {"start": v(11.17, 3.3) * mm, "end": v(12.56, 4.77) * mm});
            skLineSegment(sketch, "E64.20.0", {"start": v(11.96, 6.13) * mm, "end": v(9.93, 6.08) * mm});
            skLineSegment(sketch, "E64.20.2", {"start": v(9.93, 6.08) * mm, "end": v(10.9, 7.86) * mm});
            skLineSegment(sketch, "E64.21.0", {"start": v(9.97, 9.02) * mm, "end": v(8.02, 8.44) * mm});
            skLineSegment(sketch, "E64.21.2", {"start": v(8.02, 8.44) * mm, "end": v(8.5, 10.41) * mm});
            skLineSegment(sketch, "E64.22.0", {"start": v(7.3, 11.29) * mm, "end": v(5.56, 10.23) * mm});
            skLineSegment(sketch, "E64.22.2", {"start": v(5.56, 10.23) * mm, "end": v(5.51, 12.26) * mm});
            skLineSegment(sketch, "E64.23.0", {"start": v(4.12, 12.8) * mm, "end": v(2.73, 11.32) * mm});
            skLineSegment(sketch, "E64.23.2", {"start": v(2.73, 11.32) * mm, "end": v(2.15, 13.26) * mm});
            skPoint(sketch, "E64.center", {"position": v(0, 0) * mm});
            skArc(sketch, "E65", {"start": v(-8.31, -10.93) * mm, "mid": v(-8.08, -11.1) * mm, "end": v(-7.84, -11.27) * mm});
            skArc(sketch, "E66.trimOffspring", {"start": v(-10.86, -8.4) * mm, "mid": v(-10.68, -8.63) * mm, "end": v(-10.49, -8.86) * mm});
            skArc(sketch, "E67.trimOffspring", {"start": v(-12.66, -5.3) * mm, "mid": v(-12.55, -5.58) * mm, "end": v(-12.42, -5.84) * mm});
            skArc(sketch, "E68.trimOffspring", {"start": v(-13.6, -1.85) * mm, "mid": v(-13.56, -2.14) * mm, "end": v(-13.51, -2.43) * mm});
            skArc(sketch, "E69.trimOffspring", {"start": v(-13.62, 1.74) * mm, "mid": v(-13.65, 1.44) * mm, "end": v(-13.68, 1.15) * mm});
            skArc(sketch, "E70.trimOffspring", {"start": v(-12.7, 5.2) * mm, "mid": v(-12.81, 4.93) * mm, "end": v(-12.92, 4.65) * mm});
            skArc(sketch, "E71.trimOffspring", {"start": v(-10.93, 8.31) * mm, "mid": v(-11.1, 8.08) * mm, "end": v(-11.27, 7.84) * mm});
            skArc(sketch, "E72.trimOffspring", {"start": v(-8.4, 10.86) * mm, "mid": v(-8.63, 10.68) * mm, "end": v(-8.86, 10.49) * mm});
            skArc(sketch, "E73.trimOffspring", {"start": v(-5.3, 12.66) * mm, "mid": v(-5.58, 12.55) * mm, "end": v(-5.84, 12.42) * mm});
            skArc(sketch, "E74.trimOffspring", {"start": v(-1.85, 13.6) * mm, "mid": v(-2.14, 13.56) * mm, "end": v(-2.43, 13.51) * mm});
            skArc(sketch, "E75.trimOffspring", {"start": v(1.74, 13.62) * mm, "mid": v(1.44, 13.65) * mm, "end": v(1.15, 13.68) * mm});
            skArc(sketch, "E76.trimOffspring", {"start": v(5.2, 12.7) * mm, "mid": v(4.93, 12.81) * mm, "end": v(4.65, 12.92) * mm});
            skArc(sketch, "E77.trimOffspring", {"start": v(8.31, 10.93) * mm, "mid": v(8.08, 11.1) * mm, "end": v(7.84, 11.27) * mm});
            skArc(sketch, "E78.trimOffspring", {"start": v(10.86, 8.4) * mm, "mid": v(10.68, 8.63) * mm, "end": v(10.49, 8.86) * mm});
            skArc(sketch, "E79.trimOffspring", {"start": v(12.66, 5.3) * mm, "mid": v(12.55, 5.58) * mm, "end": v(12.42, 5.84) * mm});
            skArc(sketch, "E80.trimOffspring", {"start": v(13.6, 1.85) * mm, "mid": v(13.56, 2.14) * mm, "end": v(13.51, 2.43) * mm});
            skArc(sketch, "E81.trimOffspring", {"start": v(13.62, -1.74) * mm, "mid": v(13.65, -1.44) * mm, "end": v(13.68, -1.15) * mm});
            skArc(sketch, "E82.trimOffspring", {"start": v(12.7, -5.2) * mm, "mid": v(12.81, -4.93) * mm, "end": v(12.92, -4.65) * mm});
            skArc(sketch, "E83.trimOffspring", {"start": v(10.93, -8.31) * mm, "mid": v(11.1, -8.08) * mm, "end": v(11.27, -7.84) * mm});
            skArc(sketch, "E84.trimOffspring", {"start": v(8.4, -10.86) * mm, "mid": v(8.63, -10.68) * mm, "end": v(8.86, -10.49) * mm});
            skArc(sketch, "E85.trimOffspring", {"start": v(5.3, -12.66) * mm, "mid": v(5.58, -12.55) * mm, "end": v(5.84, -12.42) * mm});
            skArc(sketch, "E86.trimOffspring", {"start": v(1.85, -13.6) * mm, "mid": v(2.14, -13.56) * mm, "end": v(2.43, -13.51) * mm});
            skArc(sketch, "E87.trimOffspring", {"start": v(-1.74, -13.62) * mm, "mid": v(-1.44, -13.65) * mm, "end": v(-1.15, -13.68) * mm});
            skArc(sketch, "E88.trimOffspring", {"start": v(-5.2, -12.7) * mm, "mid": v(-4.93, -12.81) * mm, "end": v(-4.65, -12.92) * mm});
            skArc(sketch, "E89.filletArc", {"start": v(-12.92, 4.65) * mm, "mid": v(-12.93, 4.37) * mm, "end": v(-12.8, 4.12) * mm});
            skArc(sketch, "E90.filletArc", {"start": v(-12.26, 5.51) * mm, "mid": v(-12.53, 5.42) * mm, "end": v(-12.7, 5.2) * mm});
            skArc(sketch, "E91.filletArc", {"start": v(-11.27, 7.84) * mm, "mid": v(-11.36, 7.57) * mm, "end": v(-11.29, 7.3) * mm});
            skArc(sketch, "E92.filletArc", {"start": v(-10.41, 8.5) * mm, "mid": v(-10.7, 8.48) * mm, "end": v(-10.93, 8.31) * mm});
            skArc(sketch, "E93.filletArc", {"start": v(-8.86, 10.49) * mm, "mid": v(-9.02, 10.25) * mm, "end": v(-9.02, 9.97) * mm});
            skArc(sketch, "E94.filletArc", {"start": v(-7.86, 10.9) * mm, "mid": v(-8.14, 10.96) * mm, "end": v(-8.4, 10.86) * mm});
            skArc(sketch, "E95.filletArc", {"start": v(-5.84, 12.42) * mm, "mid": v(-6.06, 12.23) * mm, "end": v(-6.13, 11.96) * mm});
            skArc(sketch, "E96.filletArc", {"start": v(-4.77, 12.56) * mm, "mid": v(-5.02, 12.7) * mm, "end": v(-5.3, 12.66) * mm});
            skArc(sketch, "E97.filletArc", {"start": v(-2.43, 13.51) * mm, "mid": v(-2.68, 13.38) * mm, "end": v(-2.83, 13.14) * mm});
            skArc(sketch, "E98.filletArc", {"start": v(-1.35, 13.37) * mm, "mid": v(-1.57, 13.56) * mm, "end": v(-1.85, 13.6) * mm});
            skArc(sketch, "E99.filletArc", {"start": v(1.15, 13.68) * mm, "mid": v(0.87, 13.62) * mm, "end": v(0.67, 13.42) * mm});
            skArc(sketch, "E100.filletArc", {"start": v(2.15, 13.26) * mm, "mid": v(2, 13.5) * mm, "end": v(1.74, 13.62) * mm});
            skArc(sketch, "E101.filletArc", {"start": v(4.65, 12.92) * mm, "mid": v(4.37, 12.93) * mm, "end": v(4.12, 12.8) * mm});
            skArc(sketch, "E102.filletArc", {"start": v(5.51, 12.26) * mm, "mid": v(5.42, 12.53) * mm, "end": v(5.2, 12.7) * mm});
            skArc(sketch, "E103.filletArc", {"start": v(7.84, 11.27) * mm, "mid": v(7.57, 11.36) * mm, "end": v(7.3, 11.29) * mm});
            skArc(sketch, "E104.filletArc", {"start": v(8.5, 10.41) * mm, "mid": v(8.48, 10.7) * mm, "end": v(8.31, 10.93) * mm});
            skArc(sketch, "E105.filletArc", {"start": v(10.9, 7.86) * mm, "mid": v(10.96, 8.14) * mm, "end": v(10.86, 8.4) * mm});
            skArc(sketch, "E106.filletArc", {"start": v(10.49, 8.86) * mm, "mid": v(10.25, 9.02) * mm, "end": v(9.97, 9.02) * mm});
            skArc(sketch, "E107.filletArc", {"start": v(12.42, 5.84) * mm, "mid": v(12.23, 6.06) * mm, "end": v(11.96, 6.13) * mm});
            skArc(sketch, "E108.filletArc", {"start": v(12.56, 4.77) * mm, "mid": v(12.7, 5.02) * mm, "end": v(12.66, 5.3) * mm});
            skArc(sketch, "E109.filletArc", {"start": v(13.51, 2.43) * mm, "mid": v(13.38, 2.68) * mm, "end": v(13.14, 2.83) * mm});
            skArc(sketch, "E110.filletArc", {"start": v(13.37, 1.35) * mm, "mid": v(13.56, 1.57) * mm, "end": v(13.6, 1.85) * mm});
            skArc(sketch, "E111.filletArc", {"start": v(13.26, -2.15) * mm, "mid": v(13.5, -2) * mm, "end": v(13.62, -1.74) * mm});
            skArc(sketch, "E112.filletArc", {"start": v(13.68, -1.15) * mm, "mid": v(13.62, -0.87) * mm, "end": v(13.42, -0.67) * mm});
            skArc(sketch, "E113.filletArc", {"start": v(12.92, -4.65) * mm, "mid": v(12.93, -4.37) * mm, "end": v(12.8, -4.12) * mm});
            skArc(sketch, "E114.filletArc", {"start": v(12.26, -5.51) * mm, "mid": v(12.53, -5.42) * mm, "end": v(12.7, -5.2) * mm});
            skArc(sketch, "E115.filletArc", {"start": v(11.27, -7.84) * mm, "mid": v(11.36, -7.57) * mm, "end": v(11.29, -7.3) * mm});
            skArc(sketch, "E116.filletArc", {"start": v(10.41, -8.5) * mm, "mid": v(10.7, -8.48) * mm, "end": v(10.93, -8.31) * mm});
            skArc(sketch, "E117.filletArc", {"start": v(8.86, -10.49) * mm, "mid": v(9.02, -10.25) * mm, "end": v(9.02, -9.97) * mm});
            skArc(sketch, "E118.filletArc", {"start": v(7.86, -10.9) * mm, "mid": v(8.14, -10.96) * mm, "end": v(8.4, -10.86) * mm});
            skArc(sketch, "E119.filletArc", {"start": v(5.84, -12.42) * mm, "mid": v(6.06, -12.23) * mm, "end": v(6.13, -11.96) * mm});
            skArc(sketch, "E120.filletArc", {"start": v(4.77, -12.56) * mm, "mid": v(5.02, -12.7) * mm, "end": v(5.3, -12.66) * mm});
            skArc(sketch, "E121.filletArc", {"start": v(2.43, -13.51) * mm, "mid": v(2.68, -13.38) * mm, "end": v(2.83, -13.14) * mm});
            skArc(sketch, "E122.filletArc", {"start": v(1.35, -13.37) * mm, "mid": v(1.57, -13.56) * mm, "end": v(1.85, -13.6) * mm});
            skArc(sketch, "E123.filletArc", {"start": v(-1.15, -13.68) * mm, "mid": v(-0.87, -13.62) * mm, "end": v(-0.67, -13.42) * mm});
            skArc(sketch, "E124.filletArc", {"start": v(-2.15, -13.26) * mm, "mid": v(-2, -13.5) * mm, "end": v(-1.74, -13.62) * mm});
            skArc(sketch, "E125.filletArc", {"start": v(-4.65, -12.92) * mm, "mid": v(-4.37, -12.93) * mm, "end": v(-4.12, -12.8) * mm});
            skArc(sketch, "E126.filletArc", {"start": v(-5.51, -12.26) * mm, "mid": v(-5.42, -12.53) * mm, "end": v(-5.2, -12.7) * mm});
            skArc(sketch, "E127.filletArc", {"start": v(-7.84, -11.27) * mm, "mid": v(-7.57, -11.36) * mm, "end": v(-7.3, -11.29) * mm});
            skArc(sketch, "E128.filletArc", {"start": v(-8.5, -10.41) * mm, "mid": v(-8.48, -10.7) * mm, "end": v(-8.31, -10.93) * mm});
            skArc(sketch, "E129.filletArc", {"start": v(-10.49, -8.86) * mm, "mid": v(-10.25, -9.02) * mm, "end": v(-9.97, -9.02) * mm});
            skArc(sketch, "E130.filletArc", {"start": v(-10.9, -7.86) * mm, "mid": v(-10.96, -8.14) * mm, "end": v(-10.86, -8.4) * mm});
            skArc(sketch, "E131.filletArc", {"start": v(-12.42, -5.84) * mm, "mid": v(-12.23, -6.06) * mm, "end": v(-11.96, -6.13) * mm});
            skArc(sketch, "E132.filletArc", {"start": v(-12.56, -4.77) * mm, "mid": v(-12.7, -5.02) * mm, "end": v(-12.66, -5.3) * mm});
            skArc(sketch, "E133.filletArc", {"start": v(-13.51, -2.43) * mm, "mid": v(-13.38, -2.68) * mm, "end": v(-13.14, -2.83) * mm});
            skArc(sketch, "E134.filletArc", {"start": v(-13.37, -1.35) * mm, "mid": v(-13.56, -1.57) * mm, "end": v(-13.6, -1.85) * mm});
            skArc(sketch, "E135.filletArc", {"start": v(-13.68, 1.15) * mm, "mid": v(-13.62, 0.87) * mm, "end": v(-13.42, 0.67) * mm});
            skArc(sketch, "E136.filletArc", {"start": v(-13.26, 2.15) * mm, "mid": v(-13.5, 2) * mm, "end": v(-13.62, 1.74) * mm});
            skSolve(sketch);
        }
        {
            var Q0;
            Q0=makeQuery(id+"F13.imprint","IMPRINT",FACE,{"disambiguationData":[TD([[makeQuery(id+"F13.imprint","IMPRINT",EDGE,{"derivedFrom":sQuery(id+"F13.wireOp",EDGE,"E63.0")}),-1.0]])]});
            extrude(context, id + "F14", {"entities" : qUnion([Q0]), "oppositeDirection" : true, "depth" : 0.4 * mm, "offsetDistance" : 25 * mm});
        }
        {
            var Q0;
            Q0=makeQuery(id+"F14.opExtrude","CAP_FACE",FACE,{"disambiguationData":[OSD([sQuery(id+"F5.wireOp",EDGE,"E6"),sQuery(id+"F13.wireOp",EDGE,"E63.0"),sQuery(id+"F13.wireOp",EDGE,"E63.2"),sQuery(id+"F13.wireOp",EDGE,"E64.1.0"),sQuery(id+"F13.wireOp",EDGE,"E64.1.2"),sQuery(id+"F13.wireOp",EDGE,"E64.2.0"),sQuery(id+"F13.wireOp",EDGE,"E64.2.2"),sQuery(id+"F13.wireOp",EDGE,"E64.3.0"),sQuery(id+"F13.wireOp",EDGE,"E64.3.2"),sQuery(id+"F13.wireOp",EDGE,"E64.4.0"),sQuery(id+"F13.wireOp",EDGE,"E64.4.2"),sQuery(id+"F13.wireOp",EDGE,"E64.5.0"),sQuery(id+"F13.wireOp",EDGE,"E64.5.2"),sQuery(id+"F13.wireOp",EDGE,"E64.6.0"),sQuery(id+"F13.wireOp",EDGE,"E64.6.2"),sQuery(id+"F13.wireOp",EDGE,"E64.7.0"),sQuery(id+"F13.wireOp",EDGE,"E64.7.2"),sQuery(id+"F13.wireOp",EDGE,"E64.8.0"),sQuery(id+"F13.wireOp",EDGE,"E64.8.2"),sQuery(id+"F13.wireOp",EDGE,"E64.9.0"),sQuery(id+"F13.wireOp",EDGE,"E64.9.2"),sQuery(id+"F13.wireOp",EDGE,"E64.10.0"),sQuery(id+"F13.wireOp",EDGE,"E64.10.2"),sQuery(id+"F13.wireOp",EDGE,"E64.11.0"),sQuery(id+"F13.wireOp",EDGE,"E64.11.2"),sQuery(id+"F13.wireOp",EDGE,"E64.12.0"),sQuery(id+"F13.wireOp",EDGE,"E64.12.2"),sQuery(id+"F13.wireOp",EDGE,"E64.13.0"),sQuery(id+"F13.wireOp",EDGE,"E64.13.2"),sQuery(id+"F13.wireOp",EDGE,"E64.14.0"),sQuery(id+"F13.wireOp",EDGE,"E64.14.2"),sQuery(id+"F13.wireOp",EDGE,"E64.15.0"),sQuery(id+"F13.wireOp",EDGE,"E64.15.2"),sQuery(id+"F13.wireOp",EDGE,"E64.16.0"),sQuery(id+"F13.wireOp",EDGE,"E64.16.2"),sQuery(id+"F13.wireOp",EDGE,"E64.17.0"),sQuery(id+"F13.wireOp",EDGE,"E64.17.2"),sQuery(id+"F13.wireOp",EDGE,"E64.18.0"),sQuery(id+"F13.wireOp",EDGE,"E64.18.2"),sQuery(id+"F13.wireOp",EDGE,"E64.19.0"),sQuery(id+"F13.wireOp",EDGE,"E64.19.2"),sQuery(id+"F13.wireOp",EDGE,"E64.20.0"),sQuery(id+"F13.wireOp",EDGE,"E64.20.2"),sQuery(id+"F13.wireOp",EDGE,"E64.21.0"),sQuery(id+"F13.wireOp",EDGE,"E64.21.2"),sQuery(id+"F13.wireOp",EDGE,"E64.22.0"),sQuery(id+"F13.wireOp",EDGE,"E64.22.2"),sQuery(id+"F13.wireOp",EDGE,"E64.23.0"),sQuery(id+"F13.wireOp",EDGE,"E64.23.2"),sQuery(id+"F13.wireOp",EDGE,"E65"),sQuery(id+"F13.wireOp",EDGE,"E66.trimOffspring"),sQuery(id+"F13.wireOp",EDGE,"E67.trimOffspring"),sQuery(id+"F13.wireOp",EDGE,"E68.trimOffspring"),sQuery(id+"F13.wireOp",EDGE,"E69.trimOffspring"),sQuery(id+"F13.wireOp",EDGE,"E70.trimOffspring"),sQuery(id+"F13.wireOp",EDGE,"E71.trimOffspring"),sQuery(id+"F13.wireOp",EDGE,"E72.trimOffspring"),sQuery(id+"F13.wireOp",EDGE,"E73.trimOffspring"),sQuery(id+"F13.wireOp",EDGE,"E74.trimOffspring"),sQuery(id+"F13.wireOp",EDGE,"E75.trimOffspring"),sQuery(id+"F13.wireOp",EDGE,"E76.trimOffspring"),sQuery(id+"F13.wireOp",EDGE,"E77.trimOffspring"),sQuery(id+"F13.wireOp",EDGE,"E78.trimOffspring"),sQuery(id+"F13.wireOp",EDGE,"E79.trimOffspring"),sQuery(id+"F13.wireOp",EDGE,"E80.trimOffspring"),sQuery(id+"F13.wireOp",EDGE,"E81.trimOffspring"),sQuery(id+"F13.wireOp",EDGE,"E82.trimOffspring"),sQuery(id+"F13.wireOp",EDGE,"E83.trimOffspring"),sQuery(id+"F13.wireOp",EDGE,"E84.trimOffspring"),sQuery(id+"F13.wireOp",EDGE,"E85.trimOffspring"),sQuery(id+"F13.wireOp",EDGE,"E86.trimOffspring"),sQuery(id+"F13.wireOp",EDGE,"E87.trimOffspring"),sQuery(id+"F13.wireOp",EDGE,"E88.trimOffspring"),sQuery(id+"F13.wireOp",EDGE,"E89.filletArc"),sQuery(id+"F13.wireOp",EDGE,"E90.filletArc"),sQuery(id+"F13.wireOp",EDGE,"E91.filletArc"),sQuery(id+"F13.wireOp",EDGE,"E92.filletArc"),sQuery(id+"F13.wireOp",EDGE,"E93.filletArc"),sQuery(id+"F13.wireOp",EDGE,"E94.filletArc"),sQuery(id+"F13.wireOp",EDGE,"E95.filletArc"),sQuery(id+"F13.wireOp",EDGE,"E96.filletArc"),sQuery(id+"F13.wireOp",EDGE,"E97.filletArc"),sQuery(id+"F13.wireOp",EDGE,"E98.filletArc"),sQuery(id+"F13.wireOp",EDGE,"E99.filletArc"),sQuery(id+"F13.wireOp",EDGE,"E100.filletArc"),sQuery(id+"F13.wireOp",EDGE,"E101.filletArc"),sQuery(id+"F13.wireOp",EDGE,"E102.filletArc"),sQuery(id+"F13.wireOp",EDGE,"E103.filletArc"),sQuery(id+"F13.wireOp",EDGE,"E104.filletArc"),sQuery(id+"F13.wireOp",EDGE,"E105.filletArc"),sQuery(id+"F13.wireOp",EDGE,"E106.filletArc"),sQuery(id+"F13.wireOp",EDGE,"E107.filletArc"),sQuery(id+"F13.wireOp",EDGE,"E108.filletArc"),sQuery(id+"F13.wireOp",EDGE,"E109.filletArc"),sQuery(id+"F13.wireOp",EDGE,"E110.filletArc"),sQuery(id+"F13.wireOp",EDGE,"E111.filletArc"),sQuery(id+"F13.wireOp",EDGE,"E112.filletArc"),sQuery(id+"F13.wireOp",EDGE,"E113.filletArc"),sQuery(id+"F13.wireOp",EDGE,"E114.filletArc"),sQuery(id+"F13.wireOp",EDGE,"E115.filletArc"),sQuery(id+"F13.wireOp",EDGE,"E116.filletArc"),sQuery(id+"F13.wireOp",EDGE,"E117.filletArc"),sQuery(id+"F13.wireOp",EDGE,"E118.filletArc"),sQuery(id+"F13.wireOp",EDGE,"E119.filletArc"),sQuery(id+"F13.wireOp",EDGE,"E120.filletArc"),sQuery(id+"F13.wireOp",EDGE,"E121.filletArc"),sQuery(id+"F13.wireOp",EDGE,"E122.filletArc"),sQuery(id+"F13.wireOp",EDGE,"E123.filletArc"),sQuery(id+"F13.wireOp",EDGE,"E124.filletArc"),sQuery(id+"F13.wireOp",EDGE,"E125.filletArc"),sQuery(id+"F13.wireOp",EDGE,"E126.filletArc"),sQuery(id+"F13.wireOp",EDGE,"E127.filletArc"),sQuery(id+"F13.wireOp",EDGE,"E128.filletArc"),sQuery(id+"F13.wireOp",EDGE,"E129.filletArc"),sQuery(id+"F13.wireOp",EDGE,"E130.filletArc"),sQuery(id+"F13.wireOp",EDGE,"E131.filletArc"),sQuery(id+"F13.wireOp",EDGE,"E132.filletArc"),sQuery(id+"F13.wireOp",EDGE,"E133.filletArc"),sQuery(id+"F13.wireOp",EDGE,"E134.filletArc"),sQuery(id+"F13.wireOp",EDGE,"E135.filletArc"),sQuery(id+"F13.wireOp",EDGE,"E136.filletArc")])],"isStart":false});
            var Q1;
            {var subQ0=makeQuery(id+"F6.opExtrude","SWEPT_FACE",FACE,{"disambiguationData":[OSD([sQuery(id+"F5.wireOp",EDGE,"E6")])]});Q1=makeQuery(id+"F8.boolean.opBoolean","SPLIT",FACE,{"disambiguationData":[TD([subQ0])],"derivedFrom":makeQuery(id+"F6.boolean.opBoolean","SPLIT",FACE,{"disambiguationData":[TD([subQ0])],"derivedFrom":makeQuery(id+"F4.opExtrude","CAP_FACE",FACE,{"disambiguationData":[OSD([sQuery(id+"F0.wireOp",EDGE,"E0")])],"isStart":false})})});}
            extrude(context, id + "F15", {"entities" : qUnion([Q0]), "endBound" : BoundingType.UP_TO_SURFACE, "depth" : 25 * mm, "endBoundEntityFace" : qUnion([Q1]), "offsetDistance" : 25 * mm});
        }
    });
